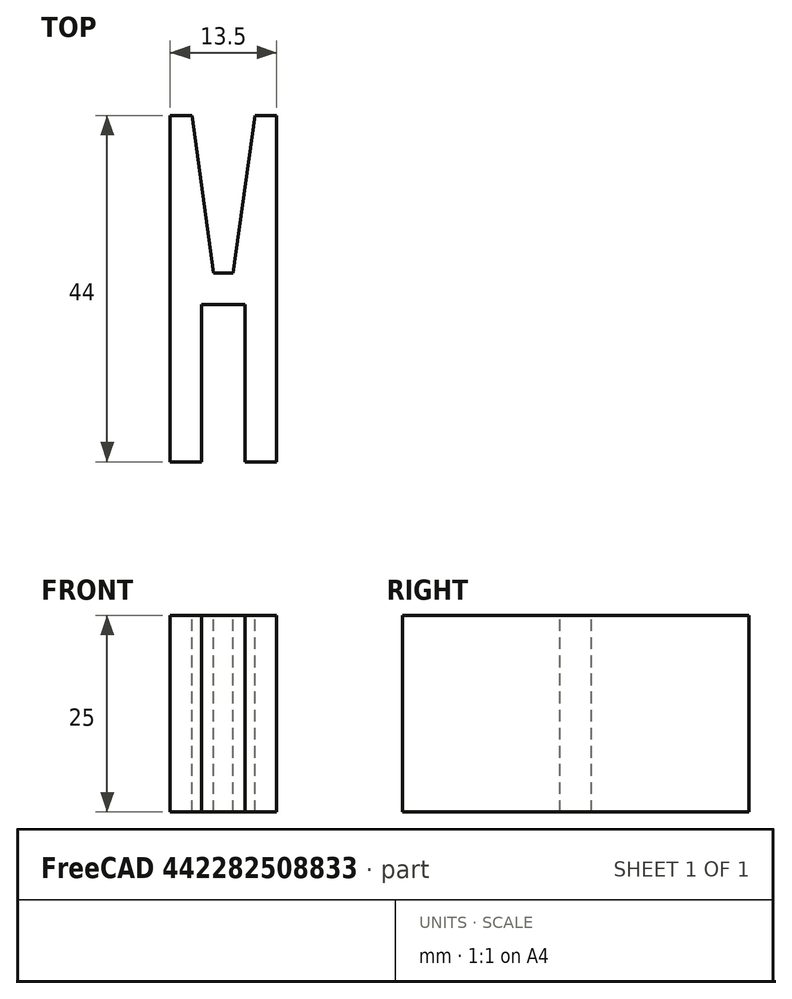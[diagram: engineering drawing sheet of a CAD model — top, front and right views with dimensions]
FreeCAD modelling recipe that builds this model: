
FCSTD DOCUMENT  (FreeCAD 0.16R)
Label: soporte caja pintura
License: All rights reserved
LicenseURL: http://en.wikipedia.org/wiki/All_rights_reserved
objects: Sketcher::SketchObject×1, PartDesign::Pad×1
note: 3 computed .brp shape members not serialized (recipe doc carries the construction recipe); baked Part::Feature solids carry a one-line shape summary decoded from their .brp

FEATURE [Sketcher::SketchObject] Sketch
  sketch-geometry (12):
    g0: LineSegment StartX=-6.75 StartY=22 StartZ=0 EndX=-6.75 EndY=-22 EndZ=0
    g1: LineSegment StartX=-6.75 StartY=-22 StartZ=0 EndX=-2.75 EndY=-22 EndZ=0
    g2: LineSegment StartX=-2.75 StartY=-22 StartZ=0 EndX=-2.75 EndY=-2 EndZ=0
    g3: LineSegment StartX=-2.75 StartY=-2 StartZ=0 EndX=2.75 EndY=-2 EndZ=0
    g4: LineSegment StartX=2.75 StartY=-2 StartZ=0 EndX=2.75 EndY=-22 EndZ=0
    g5: LineSegment StartX=2.75 StartY=-22 StartZ=0 EndX=6.75 EndY=-22 EndZ=0
    g6: LineSegment StartX=6.75 StartY=-22 StartZ=0 EndX=6.75 EndY=22 EndZ=0
    g7: LineSegment StartX=6.75 StartY=22 StartZ=0 EndX=4 EndY=22 EndZ=0
    g8: LineSegment StartX=1.25 StartY=2 StartZ=0 EndX=-1.25 EndY=2 EndZ=0
    g9: LineSegment StartX=-4 StartY=22 StartZ=0 EndX=-6.75 EndY=22 EndZ=0
    g10: LineSegment StartX=-4 StartY=22 StartZ=0 EndX=-1.25 EndY=2 EndZ=0
    g11: LineSegment StartX=4 StartY=22 StartZ=0 EndX=1.25 EndY=2 EndZ=0
  constraints (36):
    c: Vertical(g0)
    c: Coincident(g0,g1)
    c: Horizontal(g1)
    c: Coincident(g1,g2)
    c: Vertical(g2)
    c: Coincident(g2,g3)
    c: Horizontal(g3)
    c: Coincident(g3,g4)
    c: Vertical(g4)
    c: Coincident(g4,g5)
    c: Horizontal(g5)
    c: Coincident(g5,g6)
    c: Vertical(g6)
    c: Coincident(g6,g7)
    c: Horizontal(g7)
    c: Horizontal(g8)
    c: Coincident(g9,g0)
    c: Horizontal(g9)
    c: Symmetric(g0,g6,g-2)
    c: Symmetric(g3,g2,g-2)
    c: Symmetric(g8,g8,g-2)
    c: DistanceX(g3,g3) = 5.5
    c: DistanceY(g4,g4) = 20
    c: Equal(g4,g2)
    c: Equal(g5,g1)
    c: DistanceX(g1,g1) = 4
    c: DistanceY(g8,g9) = 20
    c: DistanceX(g8,g8) = 2.5
    c: DistanceX(g9,g7) = 8
    c: Symmetric(g9,g7,g-2)
    c: Coincident(g10,g9)
    c: Coincident(g10,g8)
    c: Coincident(g11,g7)
    c: Coincident(g11,g8)
    c: DistanceY(g3,g8) = 4
    c: Symmetric(g5,g6,g-1)
FEATURE [PartDesign::Pad] Pad
  Length = 25
  Length2 = 100
  Midplane = true
  Sketch = -> Sketch
  Type = 0
